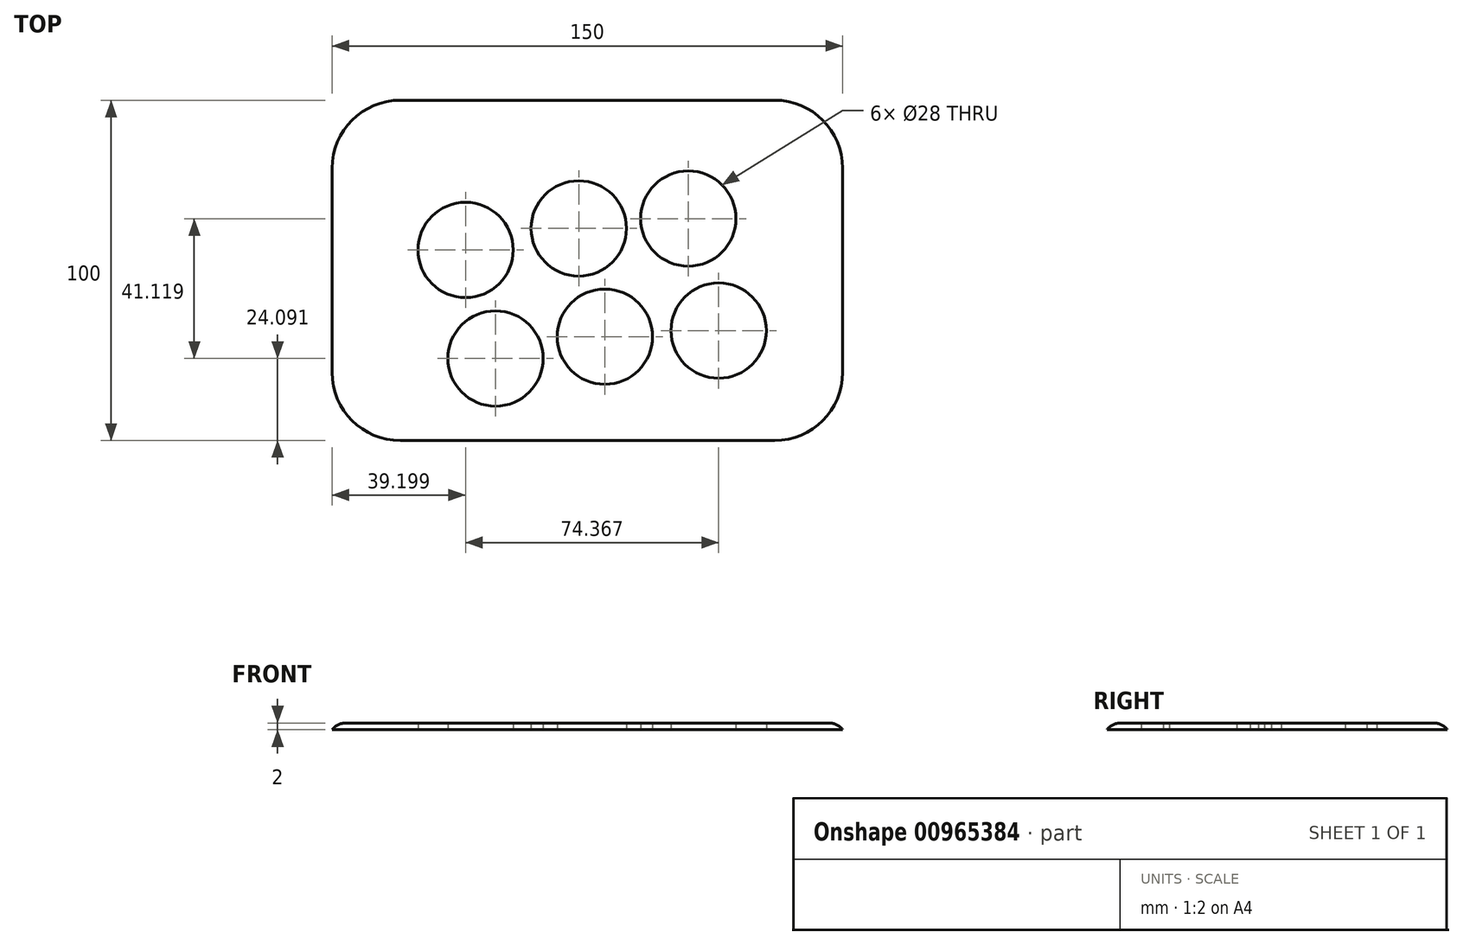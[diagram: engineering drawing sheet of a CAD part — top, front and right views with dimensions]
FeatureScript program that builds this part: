
annotation { "Feature Type Name" : "Feature", "Feature Type Description" : "" }
export const myFeature = defineFeature(function(context is Context, id is Id, definition is map)
    precondition{}
    {
        {
            var Q0;
            Q0=qCreatedBy(makeId("Top.planeOp"),FACE);
            var sketch = newSketch(context, id + "F0", { "sketchPlane" : qUnion([Q0])});
            skLineSegment(sketch, "E0.bottom", {"start": v(75, -50) * mm, "end": v(-75, -50) * mm});
            skLineSegment(sketch, "E0.top", {"start": v(75, 50) * mm, "end": v(-75, 50) * mm});
            skLineSegment(sketch, "E0.left", {"start": v(75, -50) * mm, "end": v(75, 50) * mm});
            skLineSegment(sketch, "E0.right", {"start": v(-75, -50) * mm, "end": v(-75, 50) * mm});
            skPoint(sketch, "E0.middle", {"position": v(0, 0) * mm});
            skFitSpline(sketch, "E1", {"points": [v(-75, -46.1) * mm, v(75, -18.68) * mm], "startDerivative": vector(167.08, 91.5) * mm, "endDerivative": vector(163.19, -6.81) * mm, "construction": true});
            skFitSpline(sketch, "E2", {"points": [v(-75, -6.05) * mm, v(75, 17.67) * mm], "startDerivative": vector(189.3, 67.54) * mm, "endDerivative": vector(175.28, 11.2) * mm, "construction": true});
            skPoint(sketch, "E3", {"position": v(-75, 0) * mm});
            skFitSpline(sketch, "E4", {"points": [v(-11.42, 50) * mm, v(12.82, -50) * mm], "startDerivative": vector(24.91, -106.2) * mm, "endDerivative": vector(25.66, -99.03) * mm, "construction": true});
            skFitSpline(sketch, "E5", {"points": [v(22.55, 50) * mm, v(47.54, -50) * mm], "startDerivative": vector(14.6, -99.38) * mm, "endDerivative": vector(25.49, -97.43) * mm, "construction": true});
            skFitSpline(sketch, "E6", {"points": [v(-46.95, 50) * mm, v(-24.4, -50) * mm], "startDerivative": vector(17.52, -112.04) * mm, "endDerivative": vector(-0.97, -96.46) * mm, "construction": true});
            skCircle(sketch, "E7", {"center": v(-35.8, 5.99) * mm, "radius": 14 * mm});
            skCircle(sketch, "E8", {"center": v(-2.55, 12.32) * mm, "radius": 14 * mm});
            skCircle(sketch, "E9", {"center": v(29.64, 15.2) * mm, "radius": 14 * mm});
            skCircle(sketch, "E10", {"center": v(-27, -25.9) * mm, "radius": 14 * mm});
            skCircle(sketch, "E11", {"center": v(5.13, -19.5) * mm, "radius": 14 * mm});
            skCircle(sketch, "E12", {"center": v(38.57, -17.71) * mm, "radius": 14 * mm});
            skSolve(sketch);
        }
        {
            var Q0;
            Q0=makeQuery(id+"F0.imprint","IMPRINT",FACE,{"disambiguationData":[TD([[makeQuery(id+"F0.imprint","IMPRINT",EDGE,{"derivedFrom":sQuery(id+"F0.wireOp",EDGE,"E0.bottom")}),-1.0]])]});
            extrude(context, id + "F1", {"entities" : qUnion([Q0]), "depth" : 2 * mm, "offsetDistance" : 25 * mm});
        }
        {
            var Q0;
            Q0=makeQuery(id+"F1.opExtrude","SWEPT_EDGE",EDGE,{"disambiguationData":[OSD([sQuery(id+"F0.wireOp",EDGE,"E0.bottom"),sQuery(id+"F0.wireOp",EDGE,"E0.right")])]});
            var Q1;
            Q1=makeQuery(id+"F1.opExtrude","SWEPT_EDGE",EDGE,{"disambiguationData":[OSD([sQuery(id+"F0.wireOp",EDGE,"E0.bottom"),sQuery(id+"F0.wireOp",EDGE,"E0.left")])]});
            var Q2;
            Q2=makeQuery(id+"F1.opExtrude","SWEPT_EDGE",EDGE,{"disambiguationData":[OSD([sQuery(id+"F0.wireOp",EDGE,"E0.top"),sQuery(id+"F0.wireOp",EDGE,"E0.right")])]});
            var Q3;
            Q3=makeQuery(id+"F1.opExtrude","SWEPT_EDGE",EDGE,{"disambiguationData":[OSD([sQuery(id+"F0.wireOp",EDGE,"E0.top"),sQuery(id+"F0.wireOp",EDGE,"E0.left")])]});
            fillet(context, id + "F2", {"entities" : qUnion([Q0, Q1, Q2, Q3]), "radius" : 20 * mm, "tangentPropagation" : true, "allowEdgeOverflow" : false});
        }
        {
            var Q0;
            Q0=makeQuery(id+"F1.opExtrude","CAP_EDGE",EDGE,{"disambiguationData":[OSD([sQuery(id+"F0.wireOp",EDGE,"E0.bottom")])],"isStart":false});
            var Q1;
            {var subQ0=sQuery(id+"F0.wireOp",EDGE,"E0.right");var subQ1=sQuery(id+"F0.wireOp",EDGE,"E0.bottom");Q1=makeQuery(id+"F2.opFillet","BLEND_EDGE",EDGE,{"blendedFrom":[makeQuery(id+"F1.opExtrude","SWEPT_EDGE",EDGE,{"disambiguationData":[OSD([subQ1,subQ0])]}),makeQuery(id+"F1.opExtrude","CAP_FACE",FACE,{"disambiguationData":[OSD([subQ1,sQuery(id+"F0.wireOp",EDGE,"E0.top"),sQuery(id+"F0.wireOp",EDGE,"E0.left"),subQ0,sQuery(id+"F0.wireOp",EDGE,"E7"),sQuery(id+"F0.wireOp",EDGE,"E8"),sQuery(id+"F0.wireOp",EDGE,"E9"),sQuery(id+"F0.wireOp",EDGE,"E10"),sQuery(id+"F0.wireOp",EDGE,"E11"),sQuery(id+"F0.wireOp",EDGE,"E12")])],"isStart":false})],"blendedInto":[makeQuery(id+"F1.opExtrude","CAP_FACE",FACE,{"disambiguationData":[OSD([subQ1,sQuery(id+"F0.wireOp",EDGE,"E0.top"),sQuery(id+"F0.wireOp",EDGE,"E0.left"),subQ0,sQuery(id+"F0.wireOp",EDGE,"E7"),sQuery(id+"F0.wireOp",EDGE,"E8"),sQuery(id+"F0.wireOp",EDGE,"E9"),sQuery(id+"F0.wireOp",EDGE,"E10"),sQuery(id+"F0.wireOp",EDGE,"E11"),sQuery(id+"F0.wireOp",EDGE,"E12")])],"isStart":false})]});}
            fillet(context, id + "F3", {"entities" : qUnion([Q0, Q1]), "radius" : 5 * mm, "tangentPropagation" : true, "allowEdgeOverflow" : false});
        }
    });
